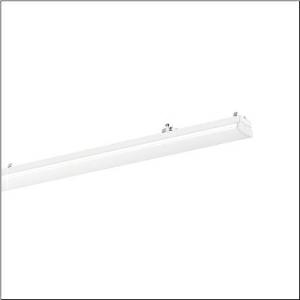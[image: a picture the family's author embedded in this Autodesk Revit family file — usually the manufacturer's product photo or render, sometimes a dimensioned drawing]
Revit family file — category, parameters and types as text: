
# Revit family: licross_r__21_recessed_opal_ho_52tl1dmn4e5m_024b
name_source: partatom
category: Lighting Fixtures
units: mm (PartAtom-declared; Revit-internal decimal feet)

## family parameters
Cut with Voids When Loaded = No
Host = Face
Light Source = No
Part Type = Normal
Room Calculation Point = No
Round Connector Dimension = Use Diameter
Shared = No

## types (1)
- --- (1 x LED, 14660 lm, 83.1 W, 4000K)
    Apparent Load = 83 VA
    CIE Flux Codes = 44 73 91 87 100
    Color Rendering = 80
    Color Temperature = 4000K
    Default Elevation = 1800 mm
    Description = Licross® 21 recessed opal HO, luminaire insert, of sheet steel, galvanised, coil coated, white, length: 1.500mm, width: 66mm, height: 67mm, LED rated luminous flux: 14.660lm, light colour: 840, control gear: ON/OFF Multilumen, with plug, 3-pole, with phase selection, mains connection: 220..240V, AC, 50/60Hz, rated input power: 83W, internal wiring halogen-free, primary optical cover: cover, of PMMA, light emission: direct with ceiling illumination distribution, primary light characteristic: symmetric, protection rating (complete): IP40, insulation class (complete): insulation class I (protective earthing), certification: CE, ENEC, VDE, UKCA, protection symbol: D if used in an environment without relevant dust loads with corresponding accessories, impact resistance: IK06, permissible ambient temperature for indoor applications: -35..+30°C, corresponds to IFS (International Featured Standards) requirements for safety and quality in the food industry, reducing of maximum allowable ambient temperature of 5°C with ceiling mounting, LABS conformity tested according to VDMA 24364:2018-05, packaging unit: 1 piece
    Height = 83 mm
    Lamp = 1 x LED
    Lamp Light Flux = 14660 lm
    Lamp Power = 83.1 W
    Lamp count = 1
    Length = 1500 mm
    Luminous efficacy = 176 lm/W
    Manufacturer = Siteco
    ModVariant = No
    Model = 52TL1DMN4E5M
    Mounting Place = Ceiling
    Mounting Type = Pendant
    Number of Poles = 1
    OnlyDefault = Yes
    Power Factor = 1
    Product Name = Licross® 21 recessed opal HO
    Product group = luminaire insert | ceiling pendant
    ProductGroupID = 902
    Protection Class = Protection class I
    Protection Degree = IP 40
    RLX_Detail_Level = 1
    RLX_Emergency_Light_Flux = 0 lm
    RLX_Emergency_Type = 0
    RLX_Emergency_Type_DB = No
    RlxData = <blob elided: 24521 chars, md5=205d728a>
    Socket = socket
    Standby Power = 0 W
    System Light Flux = 14660 lm
    System Power = 83 W
    Type Comments = factory setting: luminous flux: 100 % | (A | C | E) | 195 mA
    Type Image = l_1313666.jpg
    URL = http://relux.com
    VarID = @adj_086047
    Voltage = 0 V
    Weight = 0.00 kg
    Width = 76 mm

## geometry (parser evidence)
native form markers: Blend x4, Sweep x14
no freeform markers — native parametric forms only
